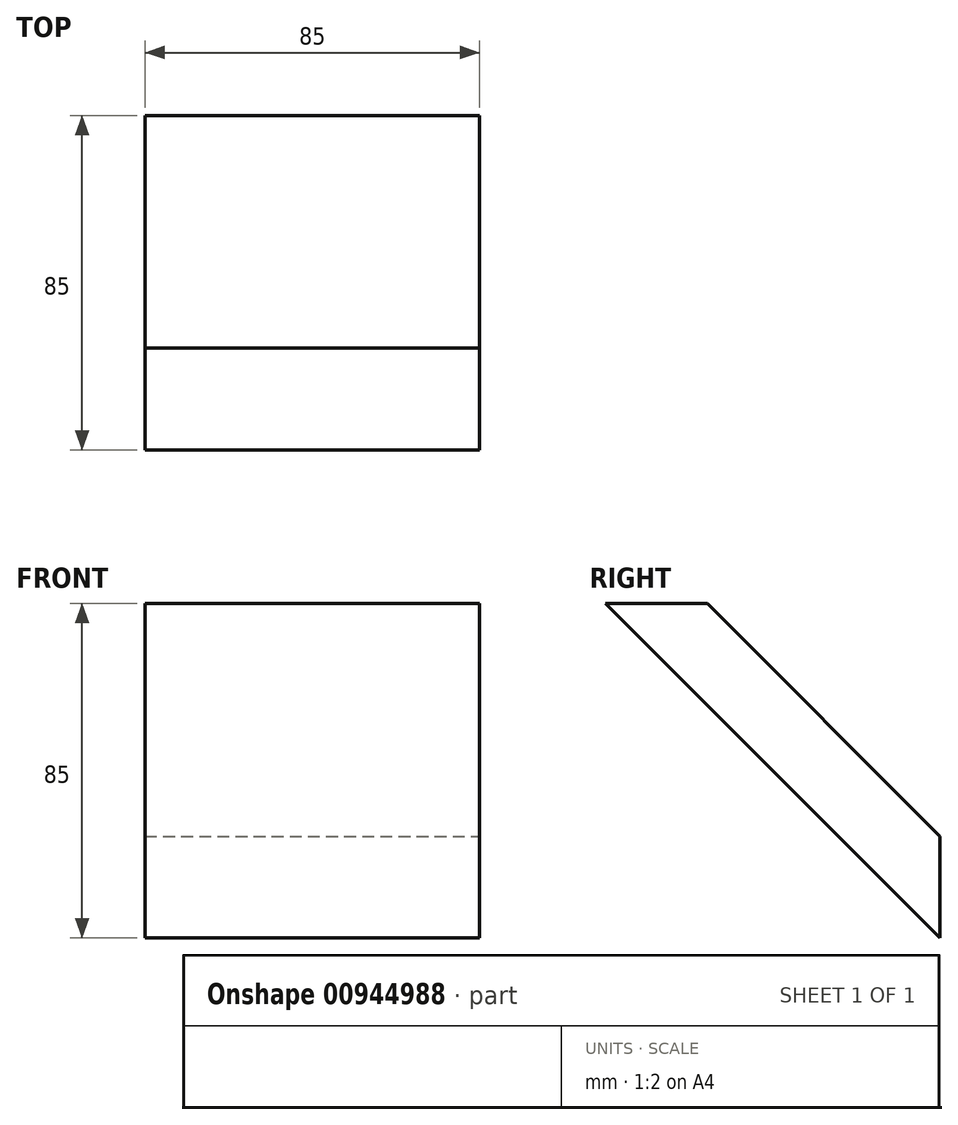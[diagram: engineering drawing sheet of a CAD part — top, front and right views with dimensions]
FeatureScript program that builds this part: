
annotation { "Feature Type Name" : "Feature", "Feature Type Description" : "" }
export const myFeature = defineFeature(function(context is Context, id is Id, definition is map)
    precondition{}
    {
        {
            var Q0;
            Q0=qCreatedBy(makeId("Top.planeOp"),FACE);
            var sketch = newSketch(context, id + "F0", { "sketchPlane" : qUnion([Q0])});
            skLineSegment(sketch, "E0.bottom", {"start": v(-42.5, 42.5) * mm, "end": v(42.5, 42.5) * mm});
            skLineSegment(sketch, "E0.top", {"start": v(-42.5, -42.5) * mm, "end": v(42.5, -42.5) * mm});
            skLineSegment(sketch, "E0.left", {"start": v(-42.5, 42.5) * mm, "end": v(-42.5, -42.5) * mm});
            skLineSegment(sketch, "E0.right", {"start": v(42.5, 42.5) * mm, "end": v(42.5, -42.5) * mm});
            skPoint(sketch, "E0.middle", {"position": v(0, 0) * mm});
            skSolve(sketch);
        }
        {
            var Q0;
            Q0 = qSketchRegion(id + "F0", true);
            extrude(context, id + "F1", {"entities" : qUnion([Q0]), "endBound" : BoundingType.SYMMETRIC, "depth" : 85 * mm, "offsetDistance" : 25 * mm});
        }
        {
            var Q0;
            Q0=qCreatedBy(makeId("Top.planeOp"),FACE);
            var sketch = newSketch(context, id + "F2", { "sketchPlane" : qUnion([Q0])});
            skLineSegment(sketch, "E1", {"start": v(0, 0) * mm, "end": v(0, 74.4) * mm, "construction": true});
            skSolve(sketch);
        }
        {
            var Q0;
            Q0=qCreatedBy(makeId("Top.planeOp"),FACE);
            var Q1;
            Q1=sQuery(id+"F2.wireOp",EDGE,"E1");
            cPlane(context, id + "F3", {"entities" : qUnion([Q0, Q1]), "cplaneType" : CPlaneType.LINE_ANGLE, "offset" : 25 * mm, "angle" : 45 * degree, "oppositeDirection" : true, "width" : 150 * mm, "height" : 150 * mm});
        }
        {
            var Q0;
            Q0=qCreatedBy(makeId("Top.planeOp"),FACE);
            var sketch = newSketch(context, id + "F4", { "sketchPlane" : qUnion([Q0])});
            skLineSegment(sketch, "E2", {"start": v(0, 0) * mm, "end": v(-92.74, 0) * mm, "construction": true});
            skSolve(sketch);
        }
        {
            var Q0;
            Q0=qCreatedBy(id+"F3.planeOp",FACE);
            var Q1;
            Q1=sQuery(id+"F4.wireOp",EDGE,"E2");
            cPlane(context, id + "F5", {"entities" : qUnion([Q0, Q1]), "cplaneType" : CPlaneType.LINE_ANGLE, "offset" : 25 * mm, "angle" : 45 * degree, "width" : 150 * mm, "height" : 150 * mm});
        }
        {
            var Q0;
            Q0=qCreatedBy(makeId("Right.planeOp"),FACE);
            var sketch = newSketch(context, id + "F6", { "sketchPlane" : qUnion([Q0])});
            skLineSegment(sketch, "E3", {"start": v(0, 0) * mm, "end": v(-49.8, 49.8) * mm});
            skLineSegment(sketch, "E4", {"start": v(-49.8, 49.8) * mm, "end": v(-49.8, -75.5) * mm});
            skLineSegment(sketch, "E5", {"start": v(-49.8, -75.5) * mm, "end": v(75.5, -75.5) * mm});
            skLineSegment(sketch, "E6", {"start": v(75.5, -75.5) * mm, "end": v(0, 0) * mm});
            skLineSegment(sketch, "E7", {"start": v(9.3, 16.57) * mm, "end": v(-34.24, 60.11) * mm});
            skLineSegment(sketch, "E8", {"start": v(-34.24, 60.11) * mm, "end": v(63.83, 60.11) * mm});
            skLineSegment(sketch, "E9", {"start": v(63.83, 60.11) * mm, "end": v(63.83, -37.96) * mm});
            skLineSegment(sketch, "E10", {"start": v(63.83, -37.96) * mm, "end": v(9.3, 16.57) * mm});
            skSolve(sketch);
        }
        {
            var Q0;
            Q0 = qSketchRegion(id + "F6", true);
            extrude(context, id + "F7", {"entities" : qUnion([Q0]), "operationType" : NewBodyOperationType.REMOVE, "endBound" : BoundingType.SYMMETRIC, "oppositeDirection" : true, "depth" : 100 * mm, "offsetDistance" : 25 * mm});
        }
    });
